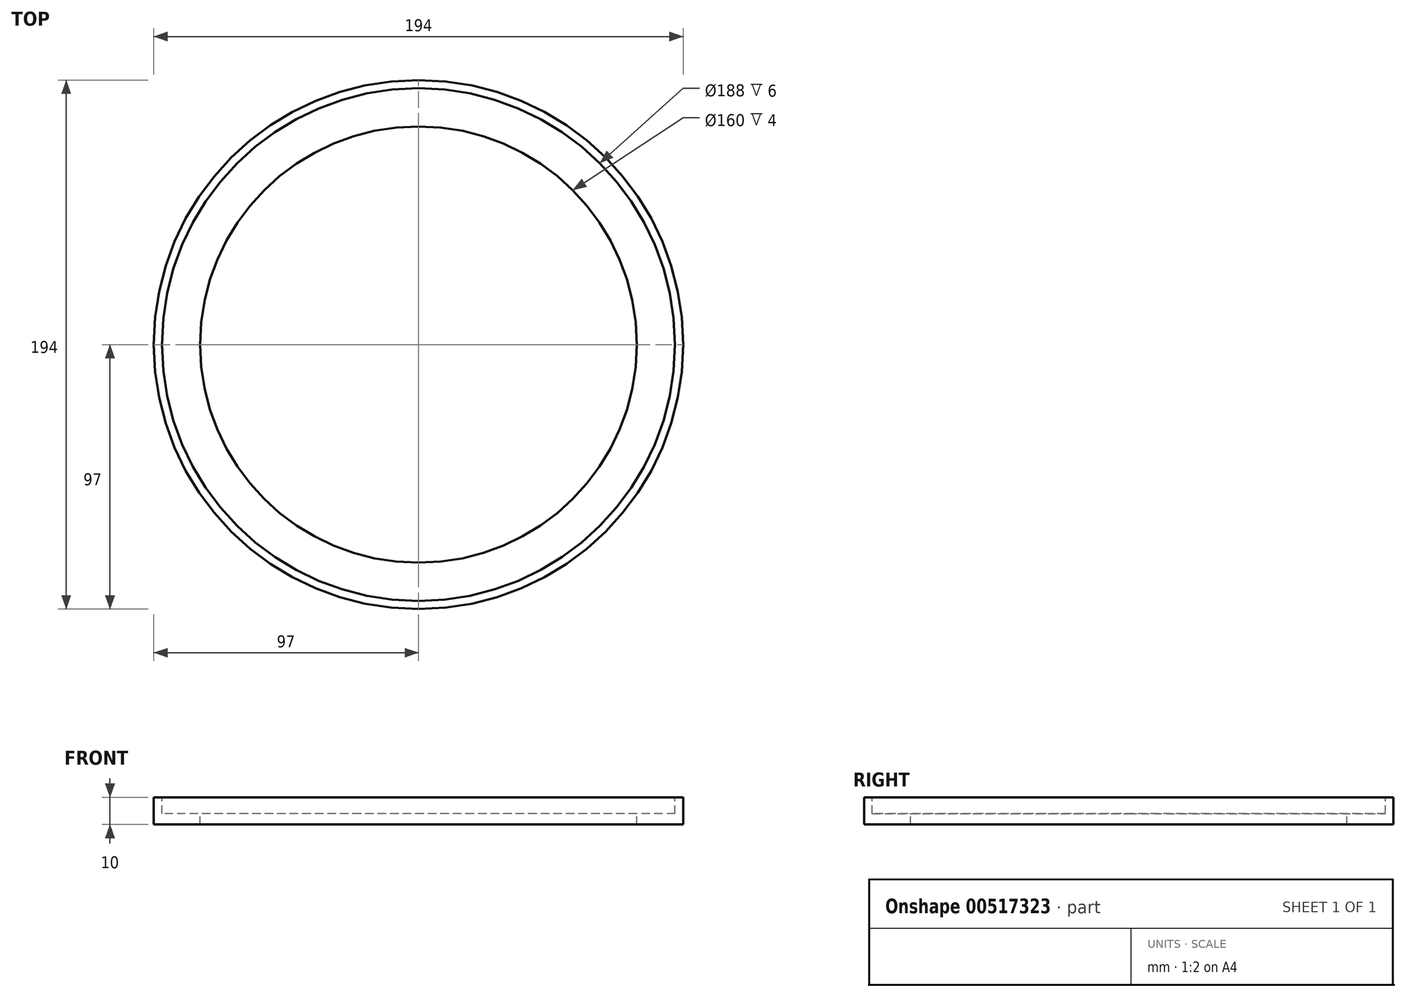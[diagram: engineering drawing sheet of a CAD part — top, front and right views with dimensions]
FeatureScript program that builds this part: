
annotation { "Feature Type Name" : "Feature", "Feature Type Description" : "" }
export const myFeature = defineFeature(function(context is Context, id is Id, definition is map)
    precondition{}
    {
        {
            var Q0;
            Q0=qCreatedBy(makeId("Front.planeOp"),FACE);
            var sketch = newSketch(context, id + "F0", { "sketchPlane" : qUnion([Q0])});
            skLineSegment(sketch, "E0.bottom", {"start": v(-94, 3) * mm, "end": v(-80, 3) * mm});
            skLineSegment(sketch, "E0.right", {"start": v(0, 3) * mm, "end": v(0, 0) * mm});
            skLineSegment(sketch, "E1.top", {"start": v(-94, 9) * mm, "end": v(-97, 9) * mm});
            skLineSegment(sketch, "E1.left", {"start": v(-94, 3) * mm, "end": v(-94, 9) * mm});
            skLineSegment(sketch, "E1.right", {"start": v(-97, 3) * mm, "end": v(-97, 9) * mm});
            skLineSegment(sketch, "E2.top", {"start": v(-97, -1) * mm, "end": v(-80, -1) * mm});
            skLineSegment(sketch, "E2.left", {"start": v(-97, 3) * mm, "end": v(-97, -1) * mm});
            skLineSegment(sketch, "E3", {"start": v(-80, 3) * mm, "end": v(-80, -1) * mm});
            skSolve(sketch);
        }
        {
            var Q0;
            Q0=makeQuery(id+"F0.imprint","IMPRINT",FACE,{"disambiguationData":[TD([[makeQuery(id+"F0.imprint","IMPRINT",EDGE,{"derivedFrom":sQuery(id+"F0.wireOp",EDGE,"E0.bottom")}),-1.0]])]});
            var Q1;
            Q1=sQuery(id+"F0.wireOp",EDGE,"E0.right");
            revolve(context, id + "F1", {"entities" : qUnion([Q0]), "axis" : qUnion([Q1]), "revolveType" : RevolveType.FULL});
        }
    });
